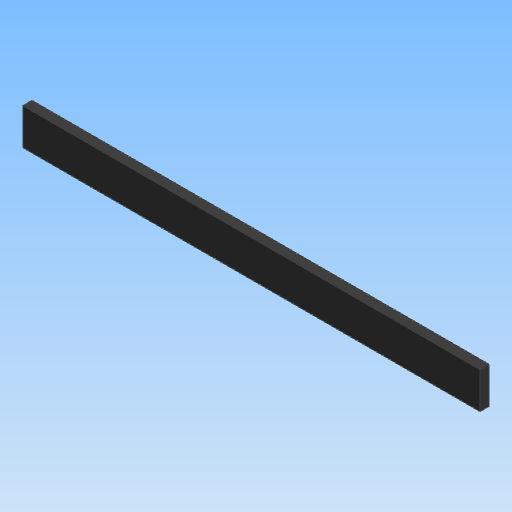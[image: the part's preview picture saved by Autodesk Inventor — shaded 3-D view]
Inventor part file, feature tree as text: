
AUTODESK INVENTOR PART (.ipt)
format: ipt  version: 2020 (Build 240168000, 168)  size: 91,648 bytes
history: native  units: mm
features: other x1, extrude x1
ambient origin geometry x8: Origin, YZ Plane, XZ Plane, XY Plane, X Axis, Y Axis, Z Axis, Center Point
bodies: Body1 (feature_tree)
feature tree (2):
  other  "實體1"
  extrude  "擠出1"  Depth=10.0mm
